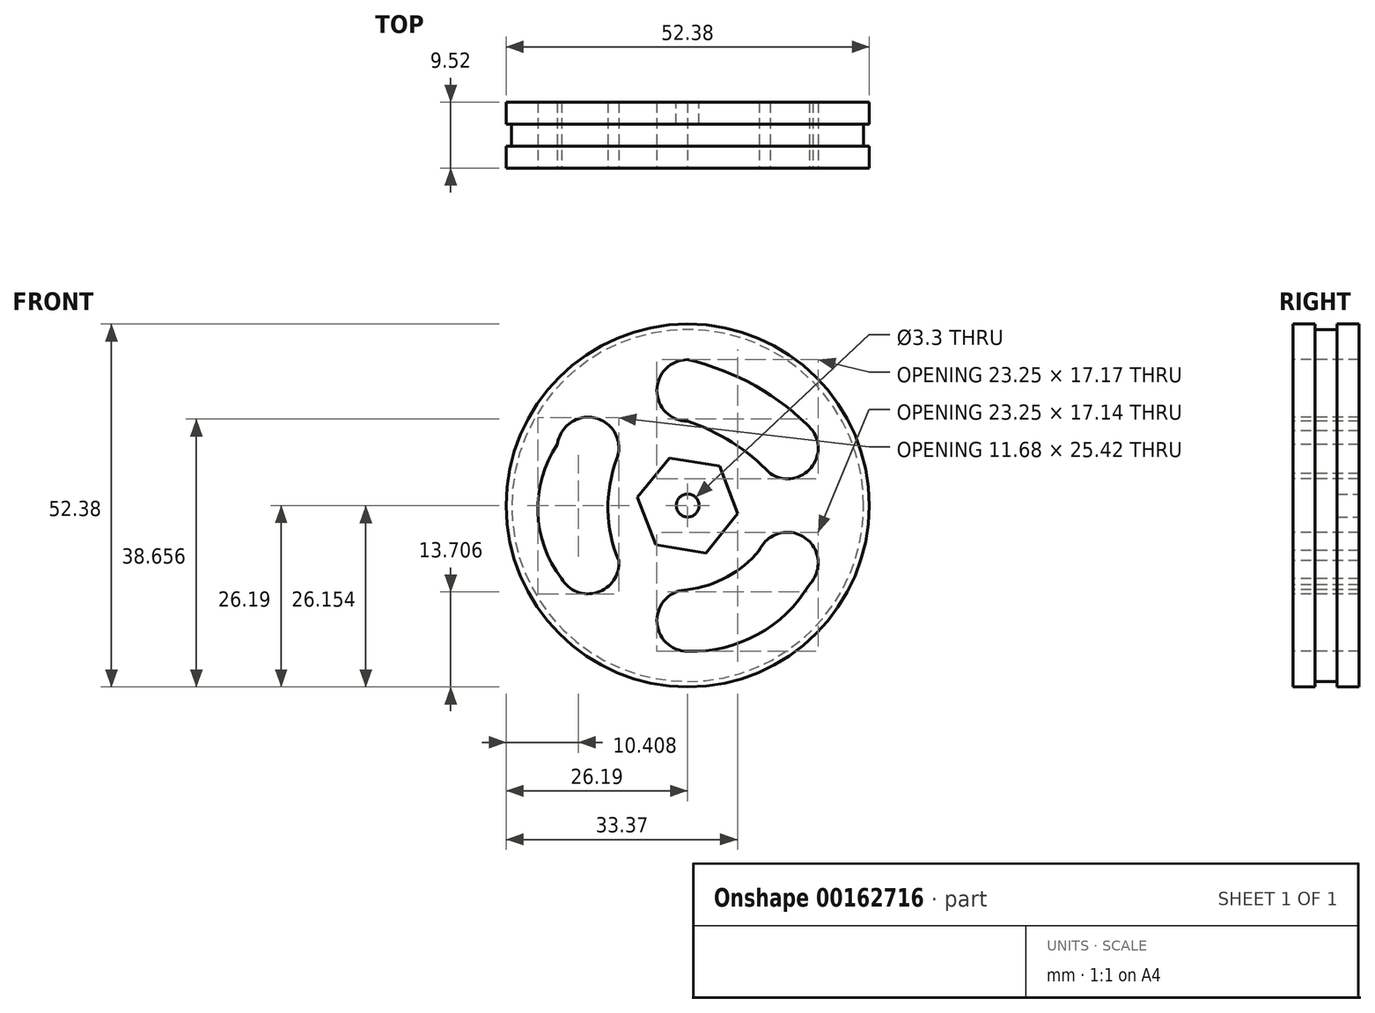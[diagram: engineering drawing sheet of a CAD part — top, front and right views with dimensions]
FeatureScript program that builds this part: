
annotation { "Feature Type Name" : "Feature", "Feature Type Description" : "" }
export const myFeature = defineFeature(function(context is Context, id is Id, definition is map)
    precondition{}
    {
        {
            var Q0;
            Q0=qCreatedBy(makeId("Front.planeOp"),FACE);
            var sketch = newSketch(context, id + "F0", { "sketchPlane" : qUnion([Q0])});
            skCircle(sketch, "E0", {"center": v(0, 0) * mm, "radius": 25.4 * mm});
            skSolve(sketch);
        }
        {
            var Q0;
            Q0 = qSketchRegion(id + "F0", true);
            extrude(context, id + "F1", {"entities" : qUnion([Q0]), "endBound" : BoundingType.SYMMETRIC, "depth" : 3.17 * mm});
        }
        {
            var Q0;
            Q0=makeQuery(id+"F1.opExtrude","CAP_FACE",FACE,{"disambiguationData":[OSD([sQuery(id+"F0.wireOp",EDGE,"E0")])],"isStart":true});
            var sketch = newSketch(context, id + "F2", { "sketchPlane" : qUnion([Q0])});
            skCircle(sketch, "E1", {"center": v(0, 0) * mm, "radius": 26.2 * mm});
            skSolve(sketch);
        }
        {
            var Q0;
            Q0 = qSketchRegion(id + "F2", true);
            extrude(context, id + "F3", {"entities" : qUnion([Q0]), "operationType" : NewBodyOperationType.ADD, "depth" : 3.17 * mm});
        }
        {
            var Q0;
            Q0=makeQuery(id+"F1.opExtrude","CAP_FACE",FACE,{"disambiguationData":[OSD([sQuery(id+"F0.wireOp",EDGE,"E0")])],"isStart":false});
            var sketch = newSketch(context, id + "F4", { "sketchPlane" : qUnion([Q0])});
            skCircle(sketch, "E2", {"center": v(0, 0) * mm, "radius": 26.2 * mm});
            skSolve(sketch);
        }
        {
            var Q0;
            Q0 = qSketchRegion(id + "F4", true);
            extrude(context, id + "F5", {"entities" : qUnion([Q0]), "operationType" : NewBodyOperationType.ADD, "depth" : 3.17 * mm});
        }
        {
            var Q0;
            Q0=makeQuery(id+"F3.opExtrude","CAP_FACE",FACE,{"disambiguationData":[OSD([sQuery(id+"F2.wireOp",EDGE,"E1")])],"isStart":false});
            var sketch = newSketch(context, id + "F6", { "sketchPlane" : qUnion([Q0])});
            skArc(sketch, "E3", {"start": v(0, -21.05) * mm, "mid": v(4.45, -16.6) * mm, "end": v(0, -12.16) * mm});
            skArc(sketch, "E4.1.0", {"start": v(10.72, -5.79) * mm, "mid": v(12, -12.05) * mm, "end": v(18.21, -10.56) * mm});
            skArc(sketch, "E4.2.0", {"start": v(18.8, 8.82) * mm, "mid": v(13.32, 12.62) * mm, "end": v(10.23, 6.71) * mm});
            skArc(sketch, "E4.3.0", {"start": v(0, 12.16) * mm, "mid": v(4.3, 17.74) * mm, "end": v(-2.18, 20.48) * mm});
            skArc(sketch, "E4.4.0", {"start": v(-16.84, 12) * mm, "mid": v(-17.55, 5.19) * mm, "end": v(-10.72, 5.78) * mm});
            skArc(sketch, "E4.5.0", {"start": v(-10.32, -6.5) * mm, "mid": v(-16.88, -4.63) * mm, "end": v(-17.55, -11.42) * mm});
            skArc(sketch, "E5", {"start": v(-10.32, -6.5) * mm, "mid": v(-5.7, -10.3) * mm, "end": v(0, -12.16) * mm});
            skArc(sketch, "E6", {"start": v(-17.55, -11.42) * mm, "mid": v(-10.1, -18.63) * mm, "end": v(0, -21.05) * mm});
            skArc(sketch, "E7", {"start": v(0, 12.16) * mm, "mid": v(-6.42, 9.1) * mm, "end": v(-11.92, 4.6) * mm});
            skArc(sketch, "E8", {"start": v(0, 21.05) * mm, "mid": v(-9.8, 17.24) * mm, "end": v(-18.08, 10.77) * mm});
            skArc(sketch, "E9", {"start": v(9.95, -7.96) * mm, "mid": v(11.5, -0.65) * mm, "end": v(10.23, 6.71) * mm});
            skArc(sketch, "E10", {"start": v(18.21, -10.56) * mm, "mid": v(21.62, -0.96) * mm, "end": v(18.8, 8.82) * mm});
            skSolve(sketch);
        }
        {
            var Q0;
            Q0=makeQuery(id+"F6.imprint","IMPRINT",FACE,{"disambiguationData":[TD([[makeQuery(id+"F6.imprint","IMPRINT",EDGE,{"derivedFrom":sQuery(id+"F6.wireOp",EDGE,"E3")}),1.0]])]});
            var Q1;
            {var subQ5=sQuery(id+"F6.wireOp",EDGE,"E4.2.0");Q1=makeQuery(id+"F6.imprint","IMPRINT",FACE,{"disambiguationData":[TD([[makeQuery(id+"F6.imprint","IMPRINT",EDGE,{"derivedFrom":subQ5}),1.0]])]});}
            var Q2;
            {var subQ0=sQuery(id+"F6.wireOp",EDGE,"E7");var subQ4=sQuery(id+"F6.wireOp",EDGE,"E4.3.0");var subQ5=makeQuery(id+"F6.imprint","INTERSECT",VERTEX,{"derivedFrom":[subQ4,subQ0]});Q2=makeQuery(id+"F6.imprint","IMPRINT",FACE,{"disambiguationData":[TD([[makeQuery(id+"F6.imprint","IMPRINT",EDGE,{"disambiguationData":[TD([[subQ5,-1.0]])],"derivedFrom":subQ4}),1.0]])]});}
            extrude(context, id + "F7", {"entities" : qUnion([Q0, Q1, Q2]), "operationType" : NewBodyOperationType.REMOVE, "endBound" : BoundingType.SYMMETRIC, "depth" : 76.2 * mm});
        }
        {
            var Q0;
            Q0=makeQuery(id+"F5.opExtrude","CAP_FACE",FACE,{"disambiguationData":[OSD([sQuery(id+"F4.wireOp",EDGE,"E2")])],"isStart":false});
            var sketch = newSketch(context, id + "F8", { "sketchPlane" : qUnion([Q0])});
            skCircle(sketch, "E11.cCircle", {"center": v(0, 0) * mm, "radius": 6.35 * mm, "construction": true});
            skLineSegment(sketch, "E11.0", {"start": v(7.24, -1.16) * mm, "end": v(2.61, -6.85) * mm});
            skLineSegment(sketch, "E11.1", {"start": v(2.61, -6.85) * mm, "end": v(-4.63, -5.69) * mm});
            skLineSegment(sketch, "E11.2", {"start": v(-4.63, -5.69) * mm, "end": v(-7.24, 1.16) * mm});
            skLineSegment(sketch, "E11.3", {"start": v(-7.24, 1.16) * mm, "end": v(-2.61, 6.85) * mm});
            skLineSegment(sketch, "E11.4", {"start": v(-2.61, 6.85) * mm, "end": v(4.63, 5.69) * mm});
            skLineSegment(sketch, "E11.5", {"start": v(4.63, 5.69) * mm, "end": v(7.24, -1.16) * mm});
            skPoint(sketch, "E11.0.midPoint", {"position": v(4.93, -4) * mm});
            skSolve(sketch);
        }
        {
            var Q0;
            Q0=makeQuery(id+"F8.imprint","IMPRINT",FACE,{"disambiguationData":[TD([[makeQuery(id+"F8.imprint","IMPRINT",EDGE,{"derivedFrom":sQuery(id+"F8.wireOp",EDGE,"E11.0")}),-1.0]])]});
            extrude(context, id + "F9", {"entities" : qUnion([Q0]), "operationType" : NewBodyOperationType.REMOVE, "oppositeDirection" : true, "depth" : 6.35 * mm});
        }
        {
            var Q0;
            Q0=makeQuery(id+"F3.opExtrude","CAP_FACE",FACE,{"disambiguationData":[OSD([sQuery(id+"F2.wireOp",EDGE,"E1")])],"isStart":false});
            var sketch = newSketch(context, id + "F10", { "sketchPlane" : qUnion([Q0])});
            skCircle(sketch, "E12", {"center": v(0, 0) * mm, "radius": 1.65 * mm});
            skSolve(sketch);
        }
        {
            var Q0;
            Q0=makeQuery(id+"F10.imprint","IMPRINT",FACE,{"disambiguationData":[TD([[makeQuery(id+"F10.imprint","IMPRINT",EDGE,{"derivedFrom":sQuery(id+"F10.wireOp",EDGE,"E12")}),1.0]])]});
            extrude(context, id + "F11", {"entities" : qUnion([Q0]), "operationType" : NewBodyOperationType.REMOVE, "oppositeDirection" : true, "depth" : 25.4 * mm});
        }
    });
